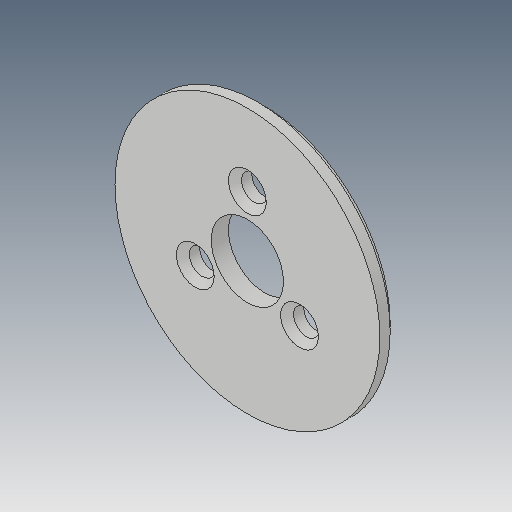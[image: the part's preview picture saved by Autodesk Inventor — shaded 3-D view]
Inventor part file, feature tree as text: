
AUTODESK INVENTOR PART (.ipt)
format: ipt  version: 2019.4 (Build 234330000, 330)  size: 115,200 bytes
history: native  units: mm
features: other x4, sketch x2, extrude x1, chamfer x1, hole x1, reference x1
ambient origin geometry x8: Origin, YZ Plane, XZ Plane, XY Plane, X Axis, Y Axis, Z Axis, Center Point
bodies: Body1 (feature_tree)
feature tree (10):
  other  "ソリッド1"
  extrude  "押し出し1"  Depth=4.2mm
  chamfer  "面取り1"  Distance=15.4mm
  hole  "穴1"  [1 undecoded]
  sketch  "スケッチ1"
  sketch  "スケッチ2"
  reference  "参照2"
  parser-record x1  (decoder bookkeeping rows leaked as tree rows — omitted from the tree; the rows remain in map.json)
  other  "BELT_SUPPORT_INNER.iam"
  other  "TIMING_BELT_P15:1"
note: 1 required parameter value undecoded (feature->parameter linkage not recoverable at this tier; creation-order binding heuristic only, values carry confidence <= 0.55)
note: 1 file-system path scrubbed to <path> (originals preserved in map.json)
